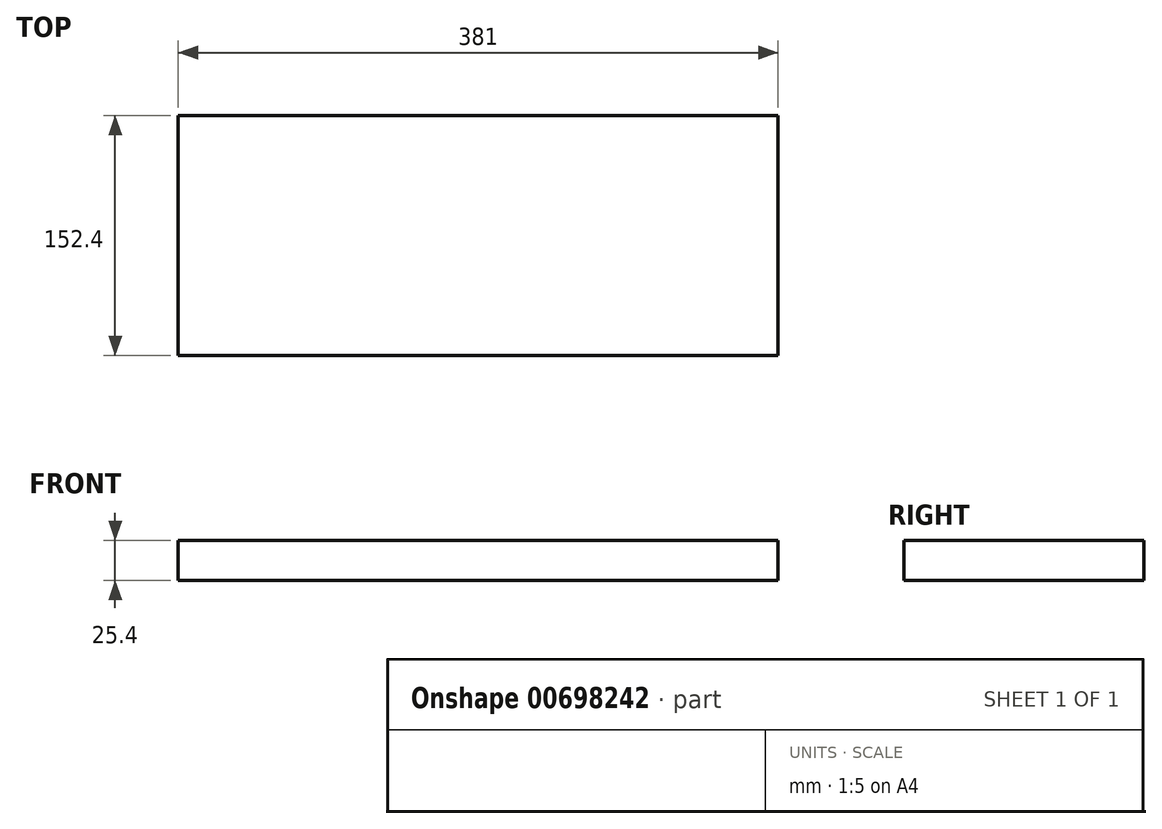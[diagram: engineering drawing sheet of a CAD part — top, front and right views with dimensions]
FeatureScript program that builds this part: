
annotation { "Feature Type Name" : "Feature", "Feature Type Description" : "" }
export const myFeature = defineFeature(function(context is Context, id is Id, definition is map)
    precondition{}
    {
        {
            var Q0;
            Q0=qCreatedBy(makeId("Top.planeOp"),FACE);
            var sketch = newSketch(context, id + "F0", { "sketchPlane" : qUnion([Q0])});
            skLineSegment(sketch, "E0.bottom", {"start": v(-199.58, 0) * mm, "end": v(181.42, 0) * mm});
            skLineSegment(sketch, "E0.top", {"start": v(-199.58, -152.4) * mm, "end": v(181.42, -152.4) * mm});
            skLineSegment(sketch, "E0.left", {"start": v(-199.58, 0) * mm, "end": v(-199.58, -152.4) * mm});
            skLineSegment(sketch, "E0.right", {"start": v(181.42, 0) * mm, "end": v(181.42, -152.4) * mm});
            skSolve(sketch);
        }
        {
            var Q0;
            Q0=makeQuery(id+"F0.imprint","IMPRINT",FACE,{"disambiguationData":[TD([[makeQuery(id+"F0.imprint","IMPRINT",EDGE,{"derivedFrom":sQuery(id+"F0.wireOp",EDGE,"E0.bottom")}),-1.0]])]});
            var sketch = newSketch(context, id + "F1", { "sketchPlane" : qUnion([Q0])});
            skSolve(sketch);
        }
        {
            var Q0;
            Q0 = qSketchRegion(id + "F1", true);
            var Q1;
            Q1=makeQuery(id+"F0.imprint","IMPRINT",FACE,{"disambiguationData":[TD([[makeQuery(id+"F0.imprint","IMPRINT",EDGE,{"derivedFrom":sQuery(id+"F0.wireOp",EDGE,"E0.bottom")}),-1.0]])]});
            extrude(context, id + "F2", {"entities" : qUnion([Q0, Q1]), "depth" : 25.4 * mm, "offsetDistance" : 25.4 * mm});
        }
    });
